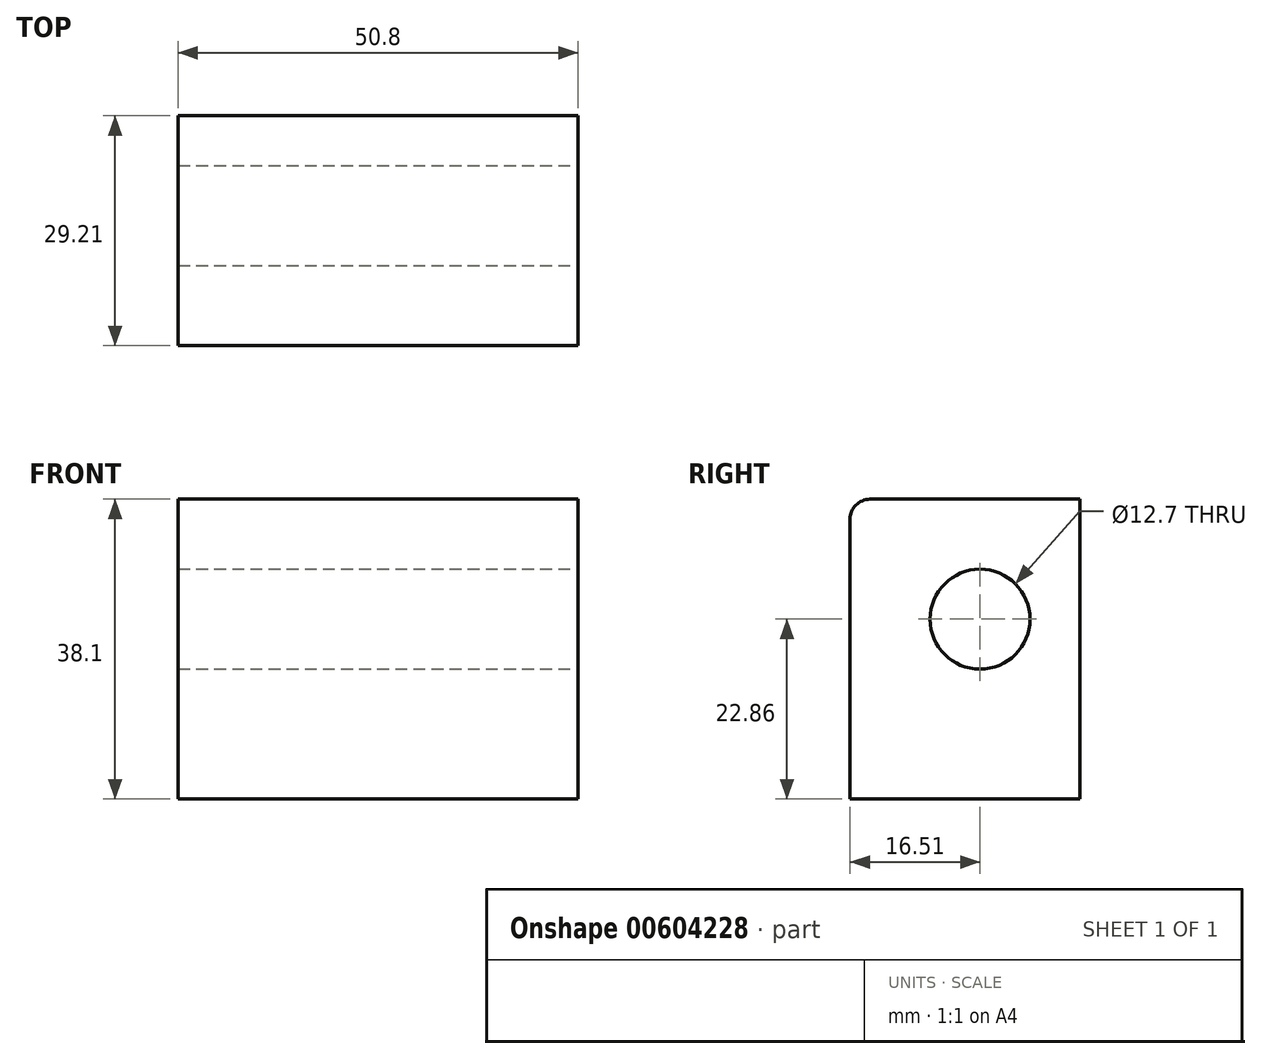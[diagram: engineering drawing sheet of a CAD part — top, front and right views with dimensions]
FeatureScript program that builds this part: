
annotation { "Feature Type Name" : "Feature", "Feature Type Description" : "" }
export const myFeature = defineFeature(function(context is Context, id is Id, definition is map)
    precondition{}
    {
        {
            var Q0;
            Q0=qCreatedBy(makeId("Front.planeOp"),FACE);
            var sketch = newSketch(context, id + "F0", { "sketchPlane" : qUnion([Q0])});
            skLineSegment(sketch, "E0.bottom", {"start": v(0, 0) * mm, "end": v(-50.8, 0) * mm});
            skLineSegment(sketch, "E0.top", {"start": v(0, -38.1) * mm, "end": v(-50.8, -38.1) * mm});
            skLineSegment(sketch, "E0.left", {"start": v(0, 0) * mm, "end": v(0, -38.1) * mm});
            skLineSegment(sketch, "E0.right", {"start": v(-50.8, 0) * mm, "end": v(-50.8, -38.1) * mm});
            skSolve(sketch);
        }
        {
            var Q0;
            Q0 = qSketchRegion(id + "F0", true);
            extrude(context, id + "F1", {"entities" : qUnion([Q0]), "depth" : 29.2 * mm, "offsetDistance" : 25.4 * mm});
        }
        {
            var Q0;
            Q0=makeQuery(id+"F1.opExtrude","CAP_EDGE",EDGE,{"disambiguationData":[OSD([sQuery(id+"F0.wireOp",EDGE,"E0.bottom")])],"isStart":false});
            fillet(context, id + "F2", {"entities" : qUnion([Q0]), "radius" : 2.54 * mm, "tangentPropagation" : true, "allowEdgeOverflow" : false});
        }
        {
            var Q0;
            Q0=makeQuery(id+"F1.opExtrude","SWEPT_FACE",FACE,{"disambiguationData":[OSD([sQuery(id+"F0.wireOp",EDGE,"E0.left")])]});
            var sketch = newSketch(context, id + "F3", { "sketchPlane" : qUnion([Q0])});
            skCircle(sketch, "E1", {"center": v(-12.7, -15.24) * mm, "radius": 6.35 * mm});
            skSolve(sketch);
        }
        {
            var Q0;
            Q0 = qSketchRegion(id + "F3", true);
            extrude(context, id + "F4", {"entities" : qUnion([Q0]), "operationType" : NewBodyOperationType.REMOVE, "endBound" : BoundingType.UP_TO_NEXT, "oppositeDirection" : true, "depth" : 51.3 * mm, "offsetDistance" : 25.4 * mm});
        }
    });
